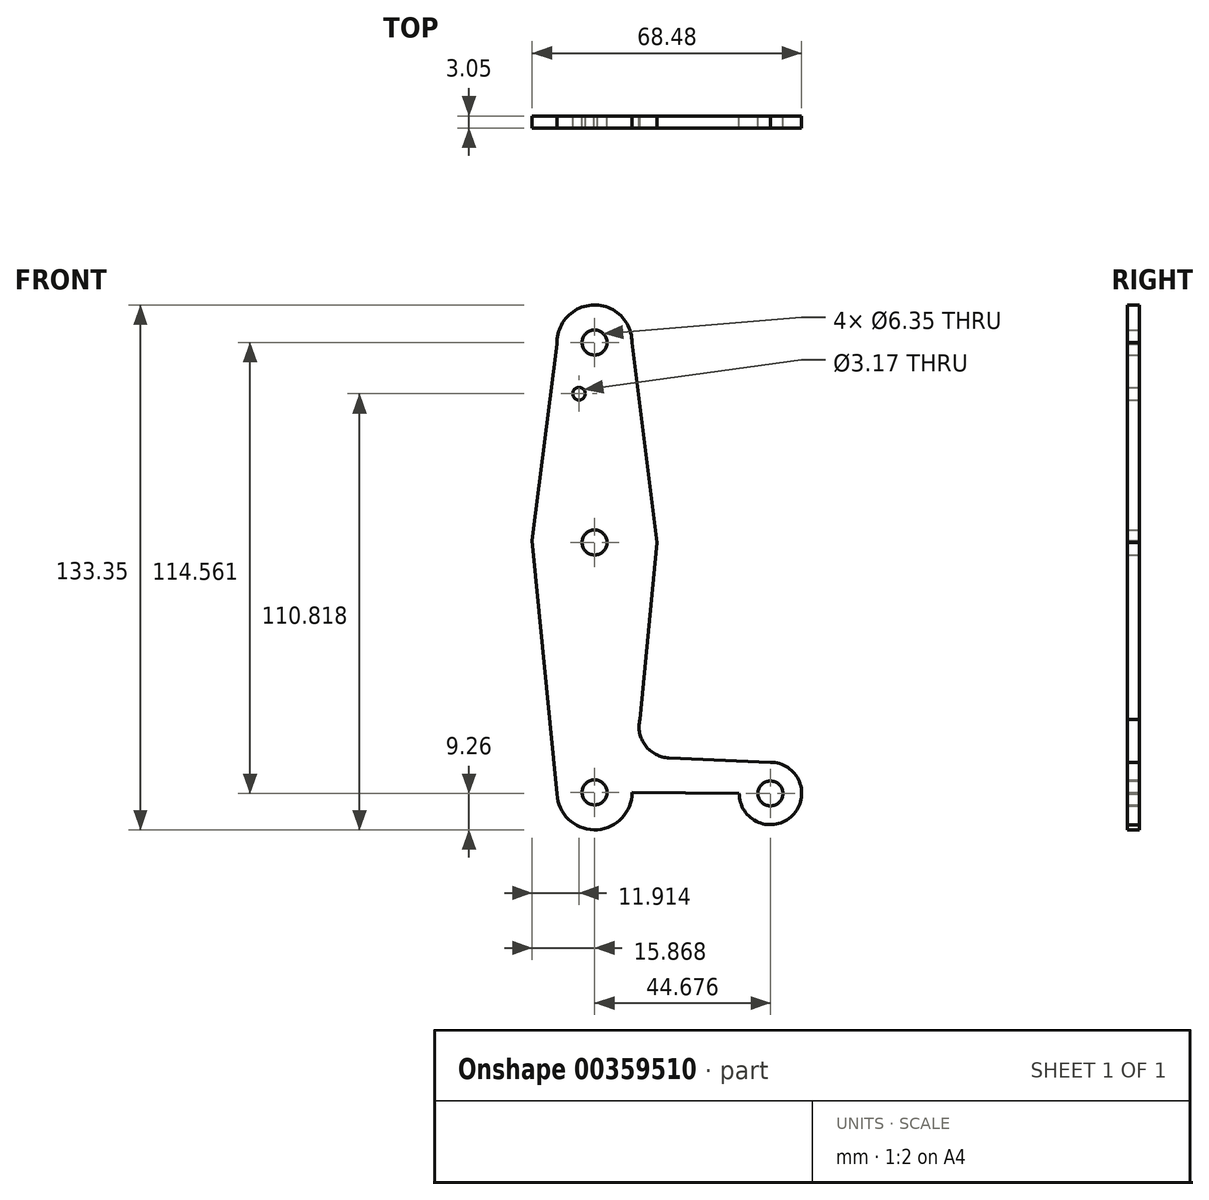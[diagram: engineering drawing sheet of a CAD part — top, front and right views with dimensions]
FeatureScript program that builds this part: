
annotation { "Feature Type Name" : "Feature", "Feature Type Description" : "" }
export const myFeature = defineFeature(function(context is Context, id is Id, definition is map)
    precondition{}
    {
        {
            var Q0;
            Q0=qCreatedBy(makeId("Front.planeOp"),FACE);
            var sketch = newSketch(context, id + "F0", { "sketchPlane" : qUnion([Q0])});
            skCircle(sketch, "E0", {"center": v(-45.05, 50.35) * mm, "radius": 9.53 * mm});
            skCircle(sketch, "E1", {"center": v(-45.05, -0.45) * mm, "radius": 15.88 * mm});
            skCircle(sketch, "E2", {"center": v(-45.05, -63.95) * mm, "radius": 9.53 * mm});
            skCircle(sketch, "E3", {"center": v(-0.38, -64.21) * mm, "radius": 7.94 * mm});
            skLineSegment(sketch, "E4", {"start": v(-45.05, -63.95) * mm, "end": v(-0.6, -64.21) * mm});
            skLineSegment(sketch, "E5", {"start": v(-45.05, 50.35) * mm, "end": v(-45.05, -63.95) * mm, "construction": true});
            skLineSegment(sketch, "E6", {"start": v(-45.05, -63.95) * mm, "end": v(-45.05, -0.45) * mm, "construction": true});
            skLineSegment(sketch, "E7", {"start": v(-54.57, 49.96) * mm, "end": v(-60.92, 0) * mm});
            skLineSegment(sketch, "E8", {"start": v(-54.57, -64.37) * mm, "end": v(-60.92, 0) * mm});
            skLineSegment(sketch, "E9", {"start": v(-45.22, -73.47) * mm, "end": v(0, -72.14) * mm});
            skCircle(sketch, "E10", {"center": v(-45.05, 50.35) * mm, "radius": 3.18 * mm});
            skCircle(sketch, "E11", {"center": v(-45.05, -0.45) * mm, "radius": 3.18 * mm});
            skCircle(sketch, "E12", {"center": v(-45.05, -63.95) * mm, "radius": 3.18 * mm});
            skCircle(sketch, "E13", {"center": v(-0.38, -64.21) * mm, "radius": 3.18 * mm});
            skLineSegment(sketch, "E14", {"start": v(-35.53, 50.35) * mm, "end": v(-29.18, -0.45) * mm});
            skLineSegment(sketch, "E15", {"start": v(-45.05, -0.45) * mm, "end": v(-45.05, 36.08) * mm, "construction": true});
            skCircle(sketch, "E16", {"center": v(-49, 37.35) * mm, "radius": 1.59 * mm});
            skArc(sketch, "E17", {"start": v(-33.53, -45.43) * mm, "mid": v(-32.14, -52.05) * mm, "end": v(-26.15, -55.2) * mm});
            skLineSegment(sketch, "E18", {"start": v(-0.38, -56.27) * mm, "end": v(-26.15, -55.2) * mm});
            skLineSegment(sketch, "E19", {"start": v(-33.53, -45.43) * mm, "end": v(-29.18, -0.45) * mm});
            skSolve(sketch);
        }
        {
            var Q0;
            Q0=makeQuery(id+"F0.imprint","IMPRINT",FACE,{"disambiguationData":[TD([[makeQuery(id+"F0.imprint","IMPRINT",EDGE,{"derivedFrom":sQuery(id+"F0.wireOp",EDGE,"E10")}),-1.0]])]});
            var Q1;
            Q1=makeQuery(id+"F0.imprint","IMPRINT",FACE,{"disambiguationData":[TD([[makeQuery(id+"F0.imprint","IMPRINT",EDGE,{"derivedFrom":sQuery(id+"F0.wireOp",EDGE,"E16")}),-1.0]])]});
            var Q2;
            Q2=makeQuery(id+"F0.imprint","IMPRINT",FACE,{"disambiguationData":[TD([[makeQuery(id+"F0.imprint","IMPRINT",EDGE,{"derivedFrom":sQuery(id+"F0.wireOp",EDGE,"E11")}),-1.0]])]});
            var Q3;
            {var subQ12=sQuery(id+"F0.wireOp",EDGE,"E17");Q3=makeQuery(id+"F0.imprint","IMPRINT",FACE,{"disambiguationData":[TD([[makeQuery(id+"F0.imprint","IMPRINT",EDGE,{"derivedFrom":subQ12}),-1.0]])]});}
            var Q4;
            Q4=makeQuery(id+"F0.imprint","IMPRINT",FACE,{"disambiguationData":[TD([[makeQuery(id+"F0.imprint","IMPRINT",EDGE,{"derivedFrom":sQuery(id+"F0.wireOp",EDGE,"E12")}),-1.0]])]});
            var Q5;
            {var subQ0=sQuery(id+"F0.wireOp",EDGE,"E9");var subQ1=sQuery(id+"F0.wireOp",EDGE,"E2");var subQ2=makeQuery(id+"F0.imprint","INTERSECT",VERTEX,{"disambiguationData":[OD(1.0)],"derivedFrom":[subQ1,subQ0]});Q5=makeQuery(id+"F0.imprint","IMPRINT",FACE,{"disambiguationData":[TD([[makeQuery(id+"F0.imprint","IMPRINT",EDGE,{"disambiguationData":[TD([[subQ2,-1.0]])],"derivedFrom":subQ1}),-1.0]])]});}
            var Q6;
            Q6=makeQuery(id+"F0.imprint","IMPRINT",FACE,{"disambiguationData":[TD([[makeQuery(id+"F0.imprint","IMPRINT",EDGE,{"derivedFrom":sQuery(id+"F0.wireOp",EDGE,"E13")}),-1.0]])]});
            extrude(context, id + "F1", {"entities" : qUnion([Q0, Q1, Q2, Q3, Q4, Q5, Q6]), "depth" : 3.05 * mm});
        }
    });
